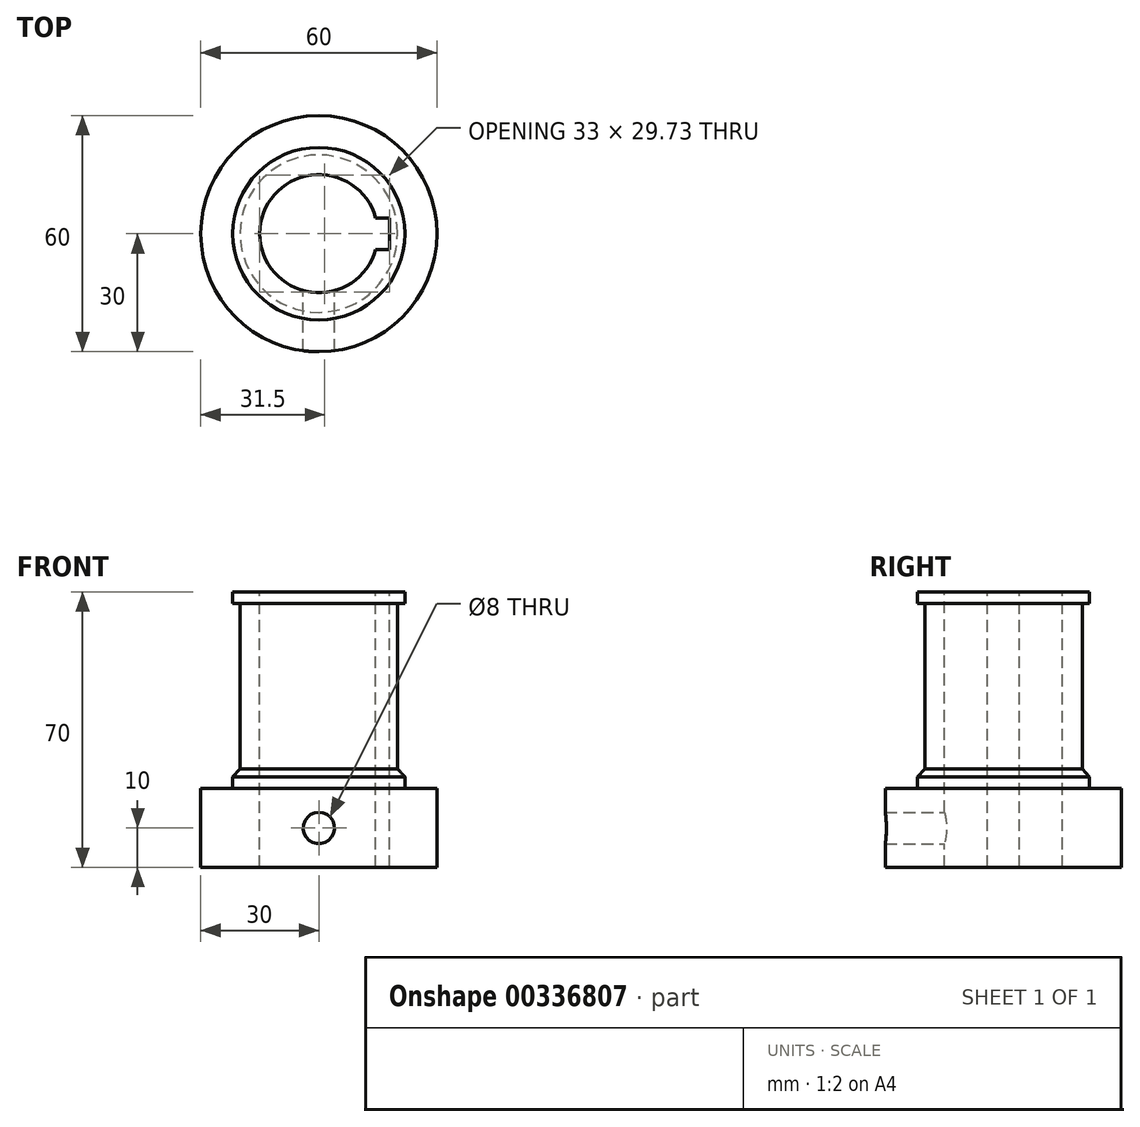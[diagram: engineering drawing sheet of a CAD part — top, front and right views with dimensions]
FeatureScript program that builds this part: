
annotation { "Feature Type Name" : "Feature", "Feature Type Description" : "" }
export const myFeature = defineFeature(function(context is Context, id is Id, definition is map)
    precondition{}
    {
        {
            var Q0;
            Q0=qCreatedBy(makeId("Top.planeOp"),FACE);
            var sketch = newSketch(context, id + "F0", { "sketchPlane" : qUnion([Q0])});
            skCircle(sketch, "E0", {"center": v(0, 0) * mm, "radius": 30 * mm});
            skSolve(sketch);
        }
        {
            var Q0;
            Q0 = qSketchRegion(id + "F0", true);
            extrude(context, id + "F1", {"entities" : qUnion([Q0]), "depth" : 20 * mm});
        }
        {
            var Q0;
            Q0=makeQuery(id+"F1.opExtrude","CAP_FACE",FACE,{"disambiguationData":[OSD([sQuery(id+"F0.wireOp",EDGE,"E0")])],"isStart":false});
            cPlane(context, id + "F2", {"entities" : qUnion([Q0]), "cplaneType" : CPlaneType.OFFSET, "offset" : 0 * mm, "width" : 150 * mm, "height" : 150 * mm});
        }
        {
            var Q0;
            Q0=qCreatedBy(id+"F2.planeOp",FACE);
            var sketch = newSketch(context, id + "F3", { "sketchPlane" : qUnion([Q0])});
            skCircle(sketch, "E1", {"center": v(0, 0) * mm, "radius": 21.9 * mm});
            skSolve(sketch);
        }
        {
            var Q0;
            Q0 = qSketchRegion(id + "F3", true);
            extrude(context, id + "F4", {"entities" : qUnion([Q0]), "operationType" : NewBodyOperationType.ADD, "depth" : 3 * mm});
        }
        {
            var Q0;
            Q0=makeQuery(id+"F4.opExtrude","CAP_FACE",FACE,{"disambiguationData":[OSD([sQuery(id+"F3.wireOp",EDGE,"E1")])],"isStart":false});
            cPlane(context, id + "F5", {"entities" : qUnion([Q0]), "cplaneType" : CPlaneType.OFFSET, "offset" : 0 * mm, "width" : 150 * mm, "height" : 150 * mm});
        }
        {
            var Q0;
            Q0=qCreatedBy(id+"F5.planeOp",FACE);
            var sketch = newSketch(context, id + "F6", { "sketchPlane" : qUnion([Q0])});
            skCircle(sketch, "E2", {"center": v(0, 0) * mm, "radius": 21.9 * mm});
            skSolve(sketch);
        }
        {
            var Q0;
            Q0 = qSketchRegion(id + "F6", true);
            extrude(context, id + "F7", {"entities" : qUnion([Q0]), "operationType" : NewBodyOperationType.ADD, "depth" : 2 * mm});
        }
        {
            var Q0;
            Q0=makeQuery(id+"F7.opExtrude","CAP_FACE",FACE,{"disambiguationData":[OSD([sQuery(id+"F6.wireOp",EDGE,"E2")])],"isStart":false});
            cPlane(context, id + "F8", {"entities" : qUnion([Q0]), "cplaneType" : CPlaneType.OFFSET, "offset" : 0 * mm, "width" : 150 * mm, "height" : 150 * mm});
        }
        {
            var Q0;
            Q0=qCreatedBy(id+"F8.planeOp",FACE);
            var sketch = newSketch(context, id + "F9", { "sketchPlane" : qUnion([Q0])});
            skCircle(sketch, "E3", {"center": v(0, 0) * mm, "radius": 20 * mm});
            skSolve(sketch);
        }
        {
            var Q0;
            Q0 = qSketchRegion(id + "F9", true);
            extrude(context, id + "F10", {"entities" : qUnion([Q0]), "operationType" : NewBodyOperationType.ADD, "depth" : 42 * mm});
        }
        {
            var Q0;
            Q0=makeQuery(id+"F7.opExtrude","CAP_EDGE",EDGE,{"disambiguationData":[OSD([sQuery(id+"F6.wireOp",EDGE,"E2")])],"isStart":false});
            chamfer(context, id + "F11", {"entities" : qUnion([Q0]), "chamferType" : ChamferType.TWO_OFFSETS, "width1" : 1.9 * mm, "oppositeDirection" : false, "width2" : 2 * mm, "tangentPropagation" : true});
        }
        {
            var Q0;
            Q0=makeQuery(id+"F10.opExtrude","CAP_FACE",FACE,{"disambiguationData":[OSD([sQuery(id+"F9.wireOp",EDGE,"E3")])],"isStart":false});
            var sketch = newSketch(context, id + "F12", { "sketchPlane" : qUnion([Q0])});
            skCircle(sketch, "E4", {"center": v(0, 0) * mm, "radius": 21.9 * mm});
            skSolve(sketch);
        }
        {
            var Q0;
            Q0 = qSketchRegion(id + "F12", true);
            extrude(context, id + "F13", {"entities" : qUnion([Q0]), "operationType" : NewBodyOperationType.ADD, "depth" : 3 * mm});
        }
        {
            var Q0;
            Q0=makeQuery(id+"F13.opExtrude","CAP_FACE",FACE,{"disambiguationData":[OSD([sQuery(id+"F12.wireOp",EDGE,"E4")])],"isStart":false});
            var sketch = newSketch(context, id + "F14", { "sketchPlane" : qUnion([Q0])});
            skArc(sketch, "E5", {"start": v(14.46, 4) * mm, "mid": v(-15, 0) * mm, "end": v(14.46, -4) * mm});
            skLineSegment(sketch, "E6", {"start": v(18, 0) * mm, "end": v(18, -4) * mm});
            skLineSegment(sketch, "E7", {"start": v(18, 0) * mm, "end": v(18, 4) * mm});
            skLineSegment(sketch, "E8", {"start": v(18, -4) * mm, "end": v(14.46, -4) * mm});
            skLineSegment(sketch, "E9", {"start": v(18, 4) * mm, "end": v(14.46, 4) * mm});
            skSolve(sketch);
        }
        {
            var Q0;
            Q0=makeQuery(id+"F14.imprint","IMPRINT",FACE,{"disambiguationData":[TD([[makeQuery(id+"F14.imprint","IMPRINT",EDGE,{"derivedFrom":sQuery(id+"F14.wireOp",EDGE,"E5")}),1.0]])]});
            extrude(context, id + "F15", {"entities" : qUnion([Q0]), "operationType" : NewBodyOperationType.REMOVE, "oppositeDirection" : true, "depth" : 78 * mm});
        }
        {
            var Q0;
            Q0=qCreatedBy(makeId("Front.planeOp"),FACE);
            var sketch = newSketch(context, id + "F16", { "sketchPlane" : qUnion([Q0])});
            skCircle(sketch, "E10", {"center": v(0, 10) * mm, "radius": 4 * mm});
            skSolve(sketch);
        }
        {
            var Q0;
            Q0=makeQuery(id+"F16.imprint","IMPRINT",FACE,{"disambiguationData":[TD([[makeQuery(id+"F16.imprint","IMPRINT",EDGE,{"derivedFrom":sQuery(id+"F16.wireOp",EDGE,"E10")}),1.0]])]});
            extrude(context, id + "F17", {"entities" : qUnion([Q0]), "operationType" : NewBodyOperationType.REMOVE, "depth" : 45 * mm});
        }
    });
